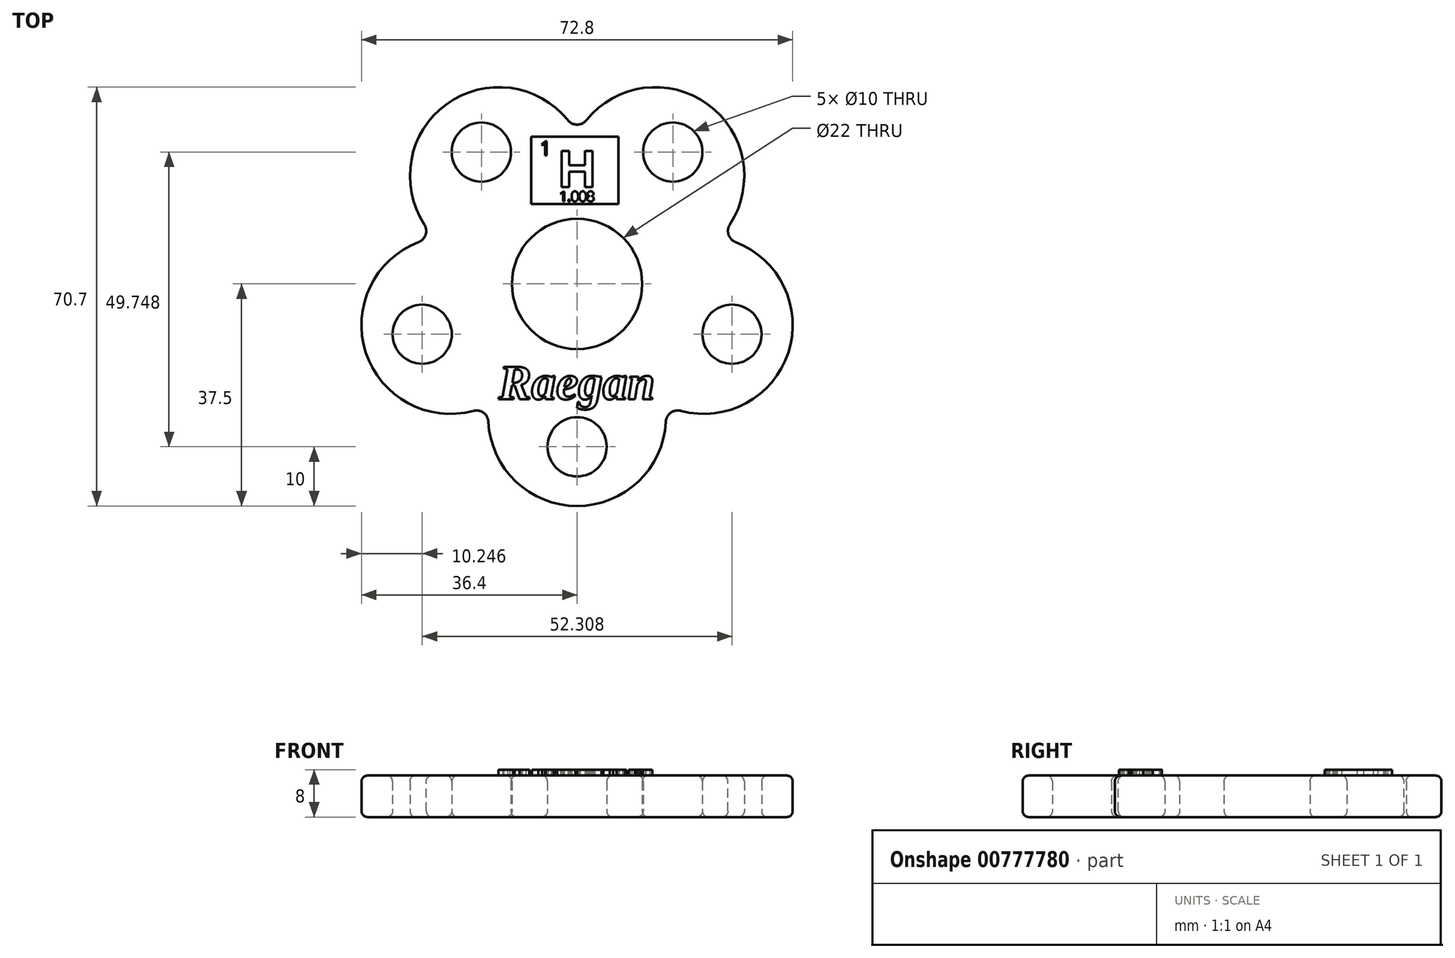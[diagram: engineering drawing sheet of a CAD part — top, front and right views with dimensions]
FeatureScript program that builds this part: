
annotation { "Feature Type Name" : "Feature", "Feature Type Description" : "" }
export const myFeature = defineFeature(function(context is Context, id is Id, definition is map)
    precondition{}
    {
        {
            var Q0;
            Q0=qCreatedBy(makeId("Top.planeOp"),FACE);
            var sketch = newSketch(context, id + "F0", { "sketchPlane" : qUnion([Q0])});
            skCircle(sketch, "E0.cCircle", {"center": v(0, 0) * mm, "radius": 22.5 * mm, "construction": true});
            skPoint(sketch, "E0.0.midPoint", {"position": v(13.23, 18.2) * mm});
            skArc(sketch, "E1", {"start": v(0, 25.28) * mm, "mid": v(-22.04, 30.34) * mm, "end": v(-24.04, 7.81) * mm});
            skArc(sketch, "E2", {"start": v(24.04, 7.81) * mm, "mid": v(22.04, 30.34) * mm, "end": v(0, 25.28) * mm});
            skArc(sketch, "E3", {"start": v(14.86, -20.45) * mm, "mid": v(35.66, -11.59) * mm, "end": v(24.04, 7.81) * mm});
            skArc(sketch, "E4", {"start": v(-14.86, -20.45) * mm, "mid": v(0, -37.5) * mm, "end": v(14.86, -20.45) * mm});
            skArc(sketch, "E5", {"start": v(-24.04, 7.81) * mm, "mid": v(-35.66, -11.59) * mm, "end": v(-14.86, -20.45) * mm});
            skCircle(sketch, "E6", {"center": v(0, 0) * mm, "radius": 25.28 * mm, "construction": true});
            skCircle(sketch, "E7", {"center": v(0, 0) * mm, "radius": 11 * mm});
            skCircle(sketch, "E8", {"center": v(-16.16, 22.25) * mm, "radius": 5 * mm});
            skCircle(sketch, "E9", {"center": v(16.16, 22.25) * mm, "radius": 5 * mm});
            skCircle(sketch, "E10", {"center": v(26.15, -8.5) * mm, "radius": 5 * mm});
            skCircle(sketch, "E11", {"center": v(0, -27.5) * mm, "radius": 5 * mm});
            skCircle(sketch, "E12", {"center": v(-26.15, -8.5) * mm, "radius": 5 * mm});
            skCircle(sketch, "E13", {"center": v(0, 0) * mm, "radius": 27.5 * mm, "construction": true});
            skLineSegment(sketch, "E14", {"start": v(0, 0) * mm, "end": v(0, 61.86) * mm, "construction": true});
            skLineSegment(sketch, "E15", {"start": v(0, 0) * mm, "end": v(37, 50.93) * mm, "construction": true});
            skLineSegment(sketch, "E16", {"start": v(0, 0) * mm, "end": v(73.63, -23.92) * mm, "construction": true});
            skLineSegment(sketch, "E17", {"start": v(0, 0) * mm, "end": v(0, -32.5) * mm, "construction": true});
            skLineSegment(sketch, "E18", {"start": v(0, 0) * mm, "end": v(-65.18, -21.18) * mm, "construction": true});
            skLineSegment(sketch, "E19", {"start": v(0, 0) * mm, "end": v(-33.66, 46.32) * mm, "construction": true});
            skSolve(sketch);
        }
        {
            var Q0;
            Q0=qSketchRegion(id+"F0",true);
            extrude(context, id + "F1", {"entities" : qUnion([Q0]), "depth" : 7 * mm, "offsetDistance" : 25.4 * mm});
        }
        {
            var Q0;
            Q0=makeQuery(id+"F1.opExtrude","SWEPT_EDGE",EDGE,{"disambiguationData":[OSD([sQuery(id+"F0.wireOp",EDGE,"E3"),sQuery(id+"F0.wireOp",EDGE,"E4")])]});
            var Q1;
            Q1=makeQuery(id+"F1.opExtrude","SWEPT_EDGE",EDGE,{"disambiguationData":[OSD([sQuery(id+"F0.wireOp",EDGE,"E2"),sQuery(id+"F0.wireOp",EDGE,"E3")])]});
            var Q2;
            Q2=makeQuery(id+"F1.opExtrude","SWEPT_EDGE",EDGE,{"disambiguationData":[OSD([sQuery(id+"F0.wireOp",EDGE,"E1"),sQuery(id+"F0.wireOp",EDGE,"E2")])]});
            var Q3;
            Q3=makeQuery(id+"F1.opExtrude","SWEPT_EDGE",EDGE,{"disambiguationData":[OSD([sQuery(id+"F0.wireOp",EDGE,"E1"),sQuery(id+"F0.wireOp",EDGE,"E5")])]});
            var Q4;
            Q4=makeQuery(id+"F1.opExtrude","SWEPT_EDGE",EDGE,{"disambiguationData":[OSD([sQuery(id+"F0.wireOp",EDGE,"E4"),sQuery(id+"F0.wireOp",EDGE,"E5")])]});
            fillet(context, id + "F2", {"entities" : qUnion([Q0, Q1, Q2, Q3, Q4]), "radius" : 2 * mm, "tangentPropagation" : true, "allowEdgeOverflow" : false});
        }
        {
            var Q0;
            Q0=makeQuery(id+"F1.opExtrude","CAP_FACE",FACE,{"disambiguationData":[OSD([sQuery(id+"F0.wireOp",EDGE,"E1"),sQuery(id+"F0.wireOp",EDGE,"E2"),sQuery(id+"F0.wireOp",EDGE,"E3"),sQuery(id+"F0.wireOp",EDGE,"E4"),sQuery(id+"F0.wireOp",EDGE,"E5"),sQuery(id+"F0.wireOp",EDGE,"E7"),sQuery(id+"F0.wireOp",EDGE,"E8"),sQuery(id+"F0.wireOp",EDGE,"E9"),sQuery(id+"F0.wireOp",EDGE,"E10"),sQuery(id+"F0.wireOp",EDGE,"E11"),sQuery(id+"F0.wireOp",EDGE,"E12")])],"isStart":false});
            var Q1;
            Q1=makeQuery(id+"F1.opExtrude","CAP_FACE",FACE,{"disambiguationData":[OSD([sQuery(id+"F0.wireOp",EDGE,"E1"),sQuery(id+"F0.wireOp",EDGE,"E2"),sQuery(id+"F0.wireOp",EDGE,"E3"),sQuery(id+"F0.wireOp",EDGE,"E4"),sQuery(id+"F0.wireOp",EDGE,"E5"),sQuery(id+"F0.wireOp",EDGE,"E7"),sQuery(id+"F0.wireOp",EDGE,"E8"),sQuery(id+"F0.wireOp",EDGE,"E9"),sQuery(id+"F0.wireOp",EDGE,"E10"),sQuery(id+"F0.wireOp",EDGE,"E11"),sQuery(id+"F0.wireOp",EDGE,"E12")])],"isStart":true});
            fillet(context, id + "F3", {"entities" : qUnion([Q0, Q1]), "radius" : 1 * mm, "tangentPropagation" : true, "allowEdgeOverflow" : false});
        }
        {
            var Q0;
            Q0=makeQuery(id+"F1.opExtrude","CAP_FACE",FACE,{"disambiguationData":[OSD([sQuery(id+"F0.wireOp",EDGE,"E1"),sQuery(id+"F0.wireOp",EDGE,"E2"),sQuery(id+"F0.wireOp",EDGE,"E3"),sQuery(id+"F0.wireOp",EDGE,"E4"),sQuery(id+"F0.wireOp",EDGE,"E5"),sQuery(id+"F0.wireOp",EDGE,"E7"),sQuery(id+"F0.wireOp",EDGE,"E8"),sQuery(id+"F0.wireOp",EDGE,"E9"),sQuery(id+"F0.wireOp",EDGE,"E10"),sQuery(id+"F0.wireOp",EDGE,"E11"),sQuery(id+"F0.wireOp",EDGE,"E12")])],"isStart":false});
            var sketch = newSketch(context, id + "F4", { "sketchPlane" : qUnion([Q0])});
            skText(sketch, "E20", { "text": "Raegan", "fontName": "Tinos-BoldItalic.ttf"});
            skLineSegment(sketch, "E21.bottom", {"start": v(-7.78, 24.86) * mm, "end": v(6.95, 24.86) * mm});
            skLineSegment(sketch, "E21.top", {"start": v(-7.78, 13.5) * mm, "end": v(6.95, 13.5) * mm});
            skLineSegment(sketch, "E21.left", {"start": v(-7.78, 24.86) * mm, "end": v(-7.78, 13.5) * mm});
            skLineSegment(sketch, "E21.right", {"start": v(6.95, 24.86) * mm, "end": v(6.95, 13.5) * mm});
            skText(sketch, "E22", { "text": "H", "fontName": "Arimo-Bold.ttf"});
            skText(sketch, "E23", { "text": "1", "fontName": "OpenSans-Regular.ttf"});
            skText(sketch, "E24", { "text": "1.008", "fontName": "OpenSans-Regular.ttf"});
            const initialGuessF4  = {"E20": [-0.01326, -0.01946, 1, 0, 0.006], "E22": [-0.00321, 0.01635, 1, 0, 0.0064], "E23": [-0.00629, 0.02169, 1, 0, 0.0024], "E24": [-0.00298, 0.01394, 1, 0, 0.00167]};
            skSetInitialGuess(sketch, initialGuessF4);
            skSolve(sketch);
        }
        {
            var Q0;
            Q0=qSketchRegion(id+"F4",true);
            extrude(context, id + "F5", {"entities" : qUnion([Q0]), "operationType" : NewBodyOperationType.ADD, "depth" : 1 * mm, "offsetDistance" : 25 * mm});
        }
    });
